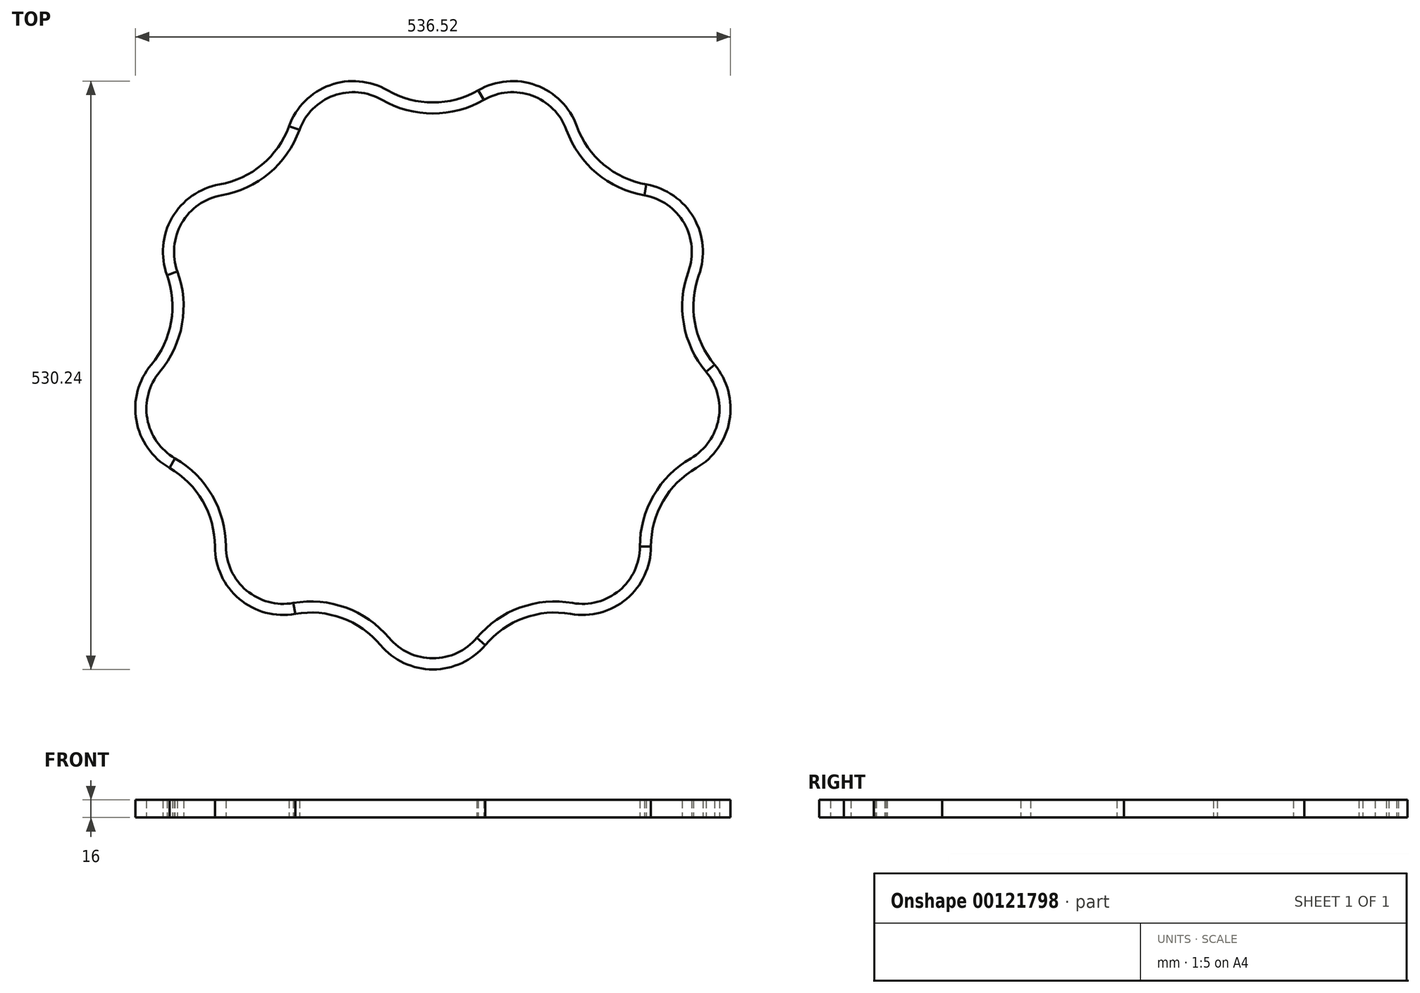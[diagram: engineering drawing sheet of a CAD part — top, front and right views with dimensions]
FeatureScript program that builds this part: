
annotation { "Feature Type Name" : "Feature", "Feature Type Description" : "" }
export const myFeature = defineFeature(function(context is Context, id is Id, definition is map)
    precondition{}
    {
        {
            var Q0;
            Q0=qCreatedBy(makeId("Top.planeOp"),FACE);
            var sketch = newSketch(context, id + "F0", { "sketchPlane" : qUnion([Q0])});
            skLineSegment(sketch, "E0", {"start": v(-1192.73, 758.28) * mm, "end": v(-1105.9, 758.28) * mm, "construction": true});
            skLineSegment(sketch, "E1", {"start": v(-1192.73, 758.28) * mm, "end": v(-1274.32, 728.59) * mm, "construction": true});
            skLineSegment(sketch, "E2", {"start": v(-1192.73, 758.28) * mm, "end": v(-1165.08, 742.32) * mm, "construction": true});
            skArc(sketch, "E3", {"start": v(-1192.73, 758.28) * mm, "mid": v(-1240.45, 762.46) * mm, "end": v(-1274.32, 728.59) * mm});
            skLineSegment(sketch, "E4", {"start": v(-1192.73, 758.28) * mm, "end": v(-1237.03, 783.86) * mm, "construction": true});
            skArc(sketch, "E5", {"start": v(-1192.73, 758.28) * mm, "mid": v(-1149.32, 746.65) * mm, "end": v(-1105.9, 758.28) * mm});
            skLineSegment(sketch, "E6", {"start": v(-1274.32, 728.59) * mm, "end": v(-1340.83, 672.78) * mm, "construction": true});
            skLineSegment(sketch, "E7", {"start": v(-1340.83, 672.78) * mm, "end": v(-1384.24, 597.58) * mm, "construction": true});
            skLineSegment(sketch, "E8", {"start": v(-1410.35, 660.52) * mm, "end": v(-1340.83, 672.78) * mm, "construction": true});
            skLineSegment(sketch, "E9", {"start": v(-1340.83, 672.78) * mm, "end": v(-1294.7, 680.9) * mm, "construction": true});
            skArc(sketch, "E10", {"start": v(-1340.83, 672.78) * mm, "mid": v(-1300.1, 691.77) * mm, "end": v(-1274.32, 728.59) * mm});
            skArc(sketch, "E11", {"start": v(-1340.83, 672.78) * mm, "mid": v(-1380.07, 645.3) * mm, "end": v(-1384.24, 597.58) * mm});
            skArc(sketch, "E12.0", {"start": v(-1190.23, 762.61) * mm, "mid": v(-1242.16, 767.15) * mm, "end": v(-1279.02, 730.3) * mm});
            skArc(sketch, "E12.1", {"start": v(-1190.23, 762.61) * mm, "mid": v(-1149.32, 751.65) * mm, "end": v(-1108.4, 762.61) * mm});
            skArc(sketch, "E13.0", {"start": v(-1195.23, 753.95) * mm, "mid": v(-1238.74, 757.76) * mm, "end": v(-1269.62, 726.88) * mm});
            skArc(sketch, "E13.1", {"start": v(-1195.23, 753.95) * mm, "mid": v(-1149.32, 741.65) * mm, "end": v(-1103.4, 753.95) * mm});
            skLineSegment(sketch, "E14", {"start": v(-1279.02, 730.3) * mm, "end": v(-1274.32, 728.59) * mm});
            skLineSegment(sketch, "E15", {"start": v(-1269.62, 726.88) * mm, "end": v(-1274.32, 728.59) * mm});
            skLineSegment(sketch, "E16", {"start": v(-1108.4, 762.61) * mm, "end": v(-1103.4, 753.95) * mm});
            skCircle(sketch, "E17", {"center": v(-1149.32, 512.08) * mm, "radius": 250 * mm, "construction": true});
            skSolve(sketch);
        }
        {
            var Q0;
            Q0=makeQuery(id+"F0.imprint","IMPRINT",FACE,{"disambiguationData":[TD([[makeQuery(id+"F0.imprint","IMPRINT",EDGE,{"derivedFrom":sQuery(id+"F0.wireOp",EDGE,"E3")}),-1.0]])]});
            var Q1;
            Q1=makeQuery(id+"F0.imprint","IMPRINT",FACE,{"disambiguationData":[TD([[makeQuery(id+"F0.imprint","IMPRINT",EDGE,{"derivedFrom":sQuery(id+"F0.wireOp",EDGE,"E3")}),1.0]])]});
            extrude(context, id + "F1", {"entities" : qUnion([Q0, Q1]), "depth" : 16 * mm});
        }
        {
            var Q0;
            Q0=makeQuery(id+"F1.opExtrude","SWEPT_BODY",BODY,{"disambiguationData":[OSD([sQuery(id+"F0.wireOp",EDGE,"E12.0"),sQuery(id+"F0.wireOp",EDGE,"E12.1"),sQuery(id+"F0.wireOp",EDGE,"E13.0"),sQuery(id+"F0.wireOp",EDGE,"E13.1"),sQuery(id+"F0.wireOp",EDGE,"E14"),sQuery(id+"F0.wireOp",EDGE,"E15"),sQuery(id+"F0.wireOp",EDGE,"E16")])]});
            var Q1;
            Q1=sQuery(id+"F0.wireOp",EDGE,"E17");
            circularPattern(context, id + "F2", {"entities" : qUnion([Q0]), "axis" : qUnion([Q1]), "angle" : 40 * degree, "instanceCount" : 9});
        }
        {
            assignVariable(context, id + "F3", {"name" : "rrad", "anyValue" : 240});
        }
    });
